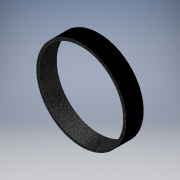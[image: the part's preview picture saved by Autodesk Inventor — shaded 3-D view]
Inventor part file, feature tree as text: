
AUTODESK INVENTOR PART (.ipt)
format: ipt  version: 2019.4 (Build 234330000, 330)  size: 107,520 bytes
history: native  units: mm
features: extrude x1, sketch x1
ambient origin geometry x8: Origin, YZ Plane, XZ Plane, XY Plane, X Axis, Y Axis, Z Axis, Center Point
bodies: Solid1 (feature_tree)
feature tree (2):
  extrude  "Extrusion1"  Depth=11.5mm
  sketch  "Sketch1"  dims[d0=58.6mm d2=1.75mm d3=11.5mm d4=0.0mm]
